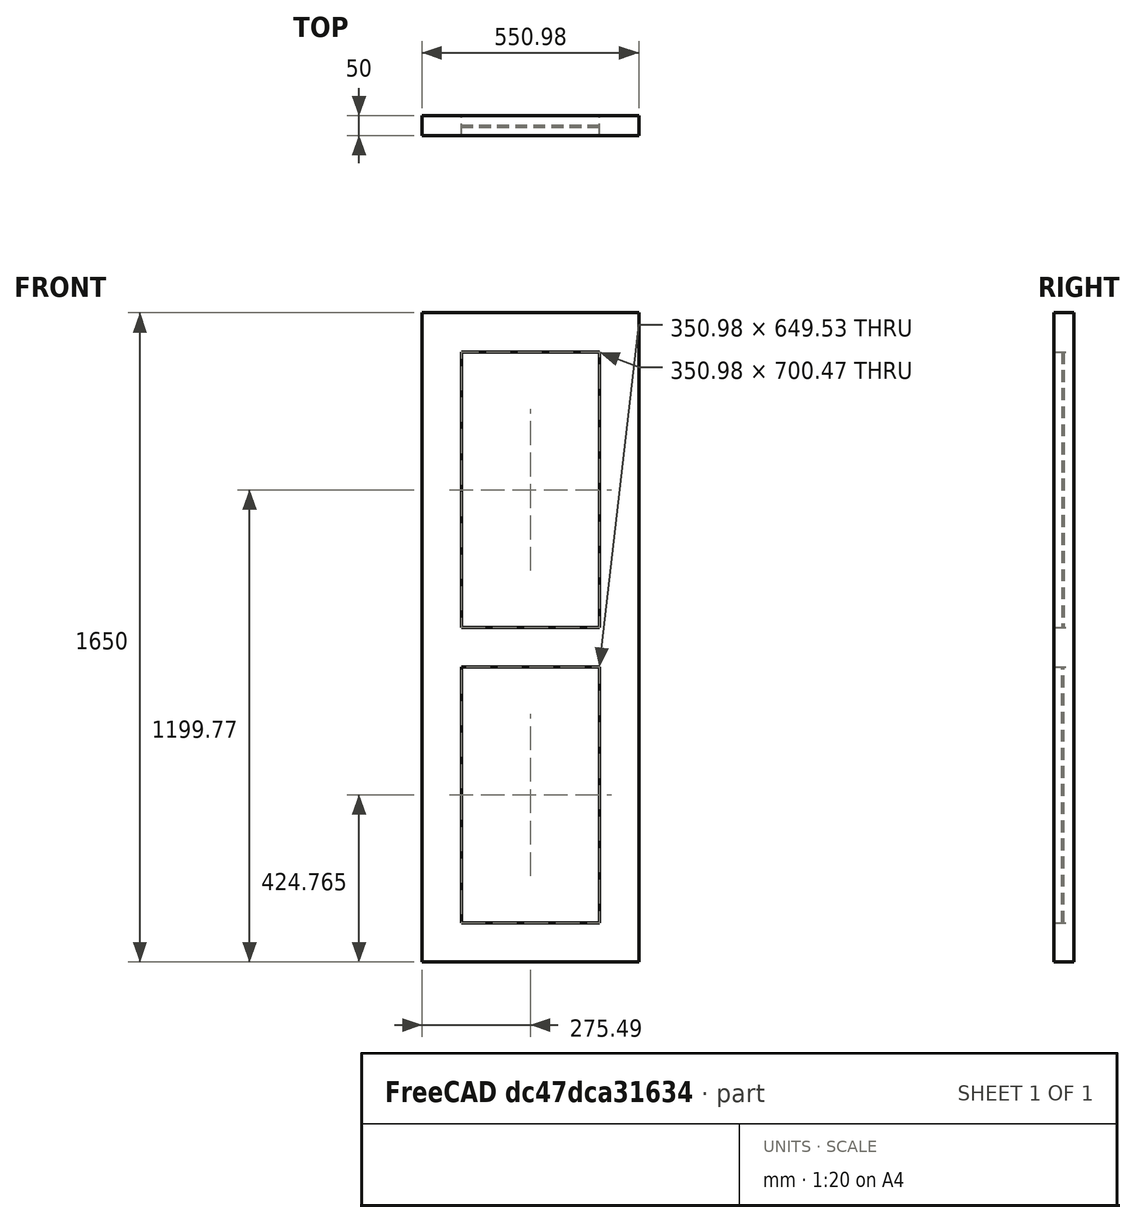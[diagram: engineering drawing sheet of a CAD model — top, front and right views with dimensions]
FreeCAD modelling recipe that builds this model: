
FCSTD DOCUMENT  (FreeCAD 0.16R6458 (Git))
Label: fixed 2 vertical-panes window
License: All rights reserved
LicenseURL: http://en.wikipedia.org/wiki/All_rights_reserved
objects: Sketcher::SketchObject×1, Part::FeaturePython×1
note: 2 computed .brp shape members not serialized (recipe doc carries the construction recipe); baked Part::Feature solids carry a one-line shape summary decoded from their .brp

FEATURE [Sketcher::SketchObject] Sketch015
  expr: Constraints[23] = Constraints.aro
  expr: Constraints.Constraint28 = Constraints.aro
  expr: Constraints.Constraint27 = Constraints.aro
  sketch-geometry (15):
    g0: LineSegment StartX=0 StartY=0 StartZ=0 EndX=-550.98 EndY=0 EndZ=0
    g1: LineSegment StartX=-550.98 StartY=0 StartZ=0 EndX=-550.98 EndY=1650 EndZ=0
    g2: LineSegment StartX=-550.98 StartY=1650 StartZ=0 EndX=0 EndY=1650 EndZ=0
    g3: LineSegment StartX=0 StartY=1650 StartZ=0 EndX=0 EndY=0 EndZ=0
    g4: LineSegment StartX=-100 StartY=1550 StartZ=0 EndX=-450.98 EndY=1550 EndZ=0
    g5: LineSegment StartX=-450.98 StartY=749.531 StartZ=0 EndX=-100 EndY=749.531 EndZ=0
    g6: LineSegment StartX=-100 StartY=849.531 StartZ=0 EndX=-450.98 EndY=849.531 EndZ=0
    g7: LineSegment StartX=-450.98 StartY=100 StartZ=0 EndX=-100 EndY=100 EndZ=0
    g8: LineSegment [constr] StartX=-450.98 StartY=749.531 StartZ=0 EndX=-450.98 EndY=849.531 EndZ=0
    g9: LineSegment [constr] StartX=-100 StartY=749.531 StartZ=0 EndX=-100 EndY=849.531 EndZ=0
    g10: LineSegment StartX=-450.98 StartY=100 StartZ=0 EndX=-450.98 EndY=749.531 EndZ=0
    g11: LineSegment StartX=-100 StartY=100 StartZ=0 EndX=-100 EndY=749.531 EndZ=0
    g12: LineSegment StartX=-100 StartY=1550 StartZ=0 EndX=-100 EndY=849.531 EndZ=0
    g13: LineSegment StartX=-450.98 StartY=1550 StartZ=0 EndX=-450.98 EndY=849.531 EndZ=0
    g14: LineSegment [constr] StartX=-100 StartY=100 StartZ=0 EndX=0 EndY=0 EndZ=0
  constraints (41):
    c: Coincident(g0,g1)
    c: Coincident(g1,g2)
    c: Coincident(g2,g3)
    c: Coincident(g3,g0)
    c: Horizontal(g0)
    c: Horizontal(g2)
    c: Vertical(g1)
    c: Vertical(g3)
    c: Coincident(g0,g-1)
    c: Horizontal(g4)
    c: Horizontal(g5)
    c: Horizontal(g6)
    c: Horizontal(g7)
    c: DistanceX(g0) = -550.98  'largura'
    c: DistanceY(g1) = 1650  'altura'
    c: Distance(g4,g1) = 100  'aro'
    c: Distance(g4,g3) = 100  'Constraint28'
    c: Distance(g4,g2) = 100  'Constraint27'
    c: Vertical(g8)  'Constraint26'
    c: Coincident(g9,g5)  'Constraint25'
    c: Vertical(g9)  'Constraint24'
    c: Coincident(g6,g9)  'Constraint23'
    c: Coincident(g6,g8)
    c: DistanceY(g5,g6) = 100
    c: Coincident(g5,g8)
    c: Coincident(g10,g7)
    c: Vertical(g10)
    c: Coincident(g11,g7)
    c: Vertical(g11)
    c: Coincident(g5,g11)
    c: Coincident(g5,g10)
    c: Coincident(g12,g4)
    c: Vertical(g12)
    c: Coincident(g13,g4)
    c: Vertical(g13)
    c: Coincident(g6,g13)
    c: Coincident(g6,g12)
    c: DistanceY(g10) = 649.531  'painel_inferior'
    c: Coincident(g14,g7)
    c: Coincident(g14,g-1)
    c: Angle(g14,g0) = 0.785398
FEATURE [Part::FeaturePython] Window003002009  label="Window"  # WARN: FeaturePython — macro-defined, semantics opaque (R4)
  Base = -> Sketch015
  Height = 0
  HoleDepth = 0
  MoveWithHost = true
  Normal = (0,0,-1)
  Placement = pos=(0,0,0) rot=(1,0,0;1.5708rad)
  Preset = 0
  Role = 0
  Width = 0
  WindowParts = aro | Frame | Wire0,Wire1,Wire2 | 50.0 | 0.0 | vidro | Glass panel | Wire1 | 5.0 | 20.0 | vidro2 | Glass panel | Wire2 | 5.0 | 20.0
